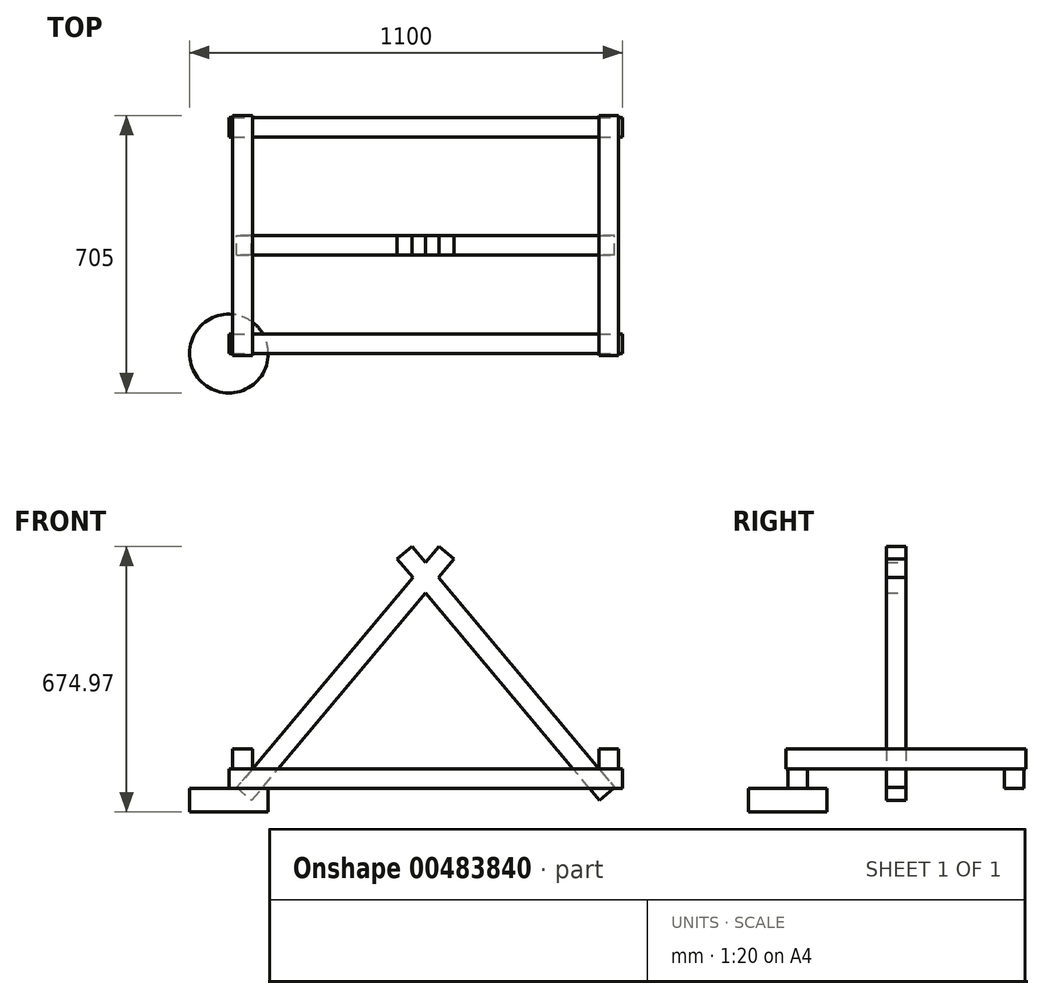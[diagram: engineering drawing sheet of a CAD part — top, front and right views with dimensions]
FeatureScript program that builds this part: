
annotation { "Feature Type Name" : "Feature", "Feature Type Description" : "" }
export const myFeature = defineFeature(function(context is Context, id is Id, definition is map)
    precondition{}
    {
        {
            var Q0;
            Q0=qCreatedBy(makeId("Top.planeOp"),FACE);
            var sketch = newSketch(context, id + "F0", { "sketchPlane" : qUnion([Q0])});
            skLineSegment(sketch, "E0.bottom", {"start": v(-500, 300) * mm, "end": v(500, 300) * mm});
            skLineSegment(sketch, "E0.top", {"start": v(-500, 250) * mm, "end": v(500, 250) * mm});
            skLineSegment(sketch, "E0.left", {"start": v(-500, 300) * mm, "end": v(-500, 250) * mm});
            skLineSegment(sketch, "E0.right", {"start": v(500, 300) * mm, "end": v(500, 250) * mm});
            skLineSegment(sketch, "E1.MirrorCS", {"start": v(500, -300) * mm, "end": v(500, -250) * mm});
            skLineSegment(sketch, "E2.MirrorCS", {"start": v(-500, -300) * mm, "end": v(-500, -250) * mm});
            skLineSegment(sketch, "E3.MirrorCS", {"start": v(-500, -300) * mm, "end": v(500, -300) * mm});
            skLineSegment(sketch, "E4.MirrorCS", {"start": v(-500, -250) * mm, "end": v(500, -250) * mm});
            skSolve(sketch);
        }
        {
            var Q0;
            Q0=makeQuery(id+"F0.imprint","IMPRINT",FACE,{"disambiguationData":[TD([[makeQuery(id+"F0.imprint","IMPRINT",EDGE,{"derivedFrom":sQuery(id+"F0.wireOp",EDGE,"E0.bottom")}),-1.0]])]});
            var Q1;
            Q1=makeQuery(id+"F0.imprint","IMPRINT",FACE,{"disambiguationData":[TD([[makeQuery(id+"F0.imprint","IMPRINT",EDGE,{"derivedFrom":sQuery(id+"F0.wireOp",EDGE,"E1.MirrorCS")}),1.0]])]});
            extrude(context, id + "F1", {"entities" : qUnion([Q0, Q1]), "depth" : 50 * mm});
        }
        {
            var Q0;
            Q0=makeQuery(id+"F1.opExtrude","CAP_FACE",FACE,{"disambiguationData":[OSD([sQuery(id+"F0.wireOp",EDGE,"E0.bottom"),sQuery(id+"F0.wireOp",EDGE,"E0.top"),sQuery(id+"F0.wireOp",EDGE,"E0.left"),sQuery(id+"F0.wireOp",EDGE,"E0.right")])],"isStart":false});
            var sketch = newSketch(context, id + "F2", { "sketchPlane" : qUnion([Q0])});
            skLineSegment(sketch, "E5.bottom", {"start": v(440, 305) * mm, "end": v(490, 305) * mm});
            skLineSegment(sketch, "E5.top", {"start": v(440, -305) * mm, "end": v(490, -305) * mm});
            skLineSegment(sketch, "E5.left", {"start": v(440, 305) * mm, "end": v(440, -305) * mm});
            skLineSegment(sketch, "E5.right", {"start": v(490, 305) * mm, "end": v(490, -305) * mm});
            skLineSegment(sketch, "E6.MirrorCS", {"start": v(-440, 305) * mm, "end": v(-440, -305) * mm});
            skLineSegment(sketch, "E7.MirrorCS", {"start": v(-490, 305) * mm, "end": v(-490, -305) * mm});
            skLineSegment(sketch, "E8.MirrorCS", {"start": v(-440, -305) * mm, "end": v(-490, -305) * mm});
            skLineSegment(sketch, "E9.MirrorCS", {"start": v(-440, 305) * mm, "end": v(-490, 305) * mm});
            skSolve(sketch);
        }
        {
            var Q0;
            {var subQ0=sQuery(id+"F2.wireOp",EDGE,"E8.MirrorCS");Q0=makeQuery(id+"F2.imprint","IMPRINT",FACE,{"disambiguationData":[TD([[makeQuery(id+"F2.imprint","IMPRINT",EDGE,{"derivedFrom":subQ0}),-1.0]])]});}
            var Q1;
            {var subQ0=sQuery(id+"F2.wireOp",EDGE,"E5.top");Q1=makeQuery(id+"F2.imprint","IMPRINT",FACE,{"disambiguationData":[TD([[makeQuery(id+"F2.imprint","IMPRINT",EDGE,{"derivedFrom":subQ0}),1.0]])]});}
            var Q2;
            {var subQ0=sQuery(id+"F2.wireOp",EDGE,"E6.MirrorCS");var subQ1=makeQuery(id+"F1.opExtrude","CAP_EDGE",EDGE,{"disambiguationData":[OSD([sQuery(id+"F0.wireOp",EDGE,"E0.bottom")])],"isStart":false});var subQ2=makeQuery(id+"F2.imprint","INTERSECT",VERTEX,{"derivedFrom":[subQ1,subQ0]});Q2=makeQuery(id+"F2.imprint","IMPRINT",FACE,{"disambiguationData":[TD([[makeQuery(id+"F2.imprint","IMPRINT",EDGE,{"disambiguationData":[TD([[subQ2,-1.0]])],"derivedFrom":subQ0}),-1.0]])]});}
            var Q3;
            {var subQ0=sQuery(id+"F2.wireOp",EDGE,"E5.left");var subQ1=makeQuery(id+"F1.opExtrude","CAP_EDGE",EDGE,{"disambiguationData":[OSD([sQuery(id+"F0.wireOp",EDGE,"E0.bottom")])],"isStart":false});var subQ2=makeQuery(id+"F2.imprint","INTERSECT",VERTEX,{"derivedFrom":[subQ1,subQ0]});Q3=makeQuery(id+"F2.imprint","IMPRINT",FACE,{"disambiguationData":[TD([[makeQuery(id+"F2.imprint","IMPRINT",EDGE,{"disambiguationData":[TD([[subQ2,-1.0]])],"derivedFrom":subQ0}),1.0]])]});}
            var Q4;
            {var subQ0=sQuery(id+"F2.wireOp",EDGE,"E9.MirrorCS");Q4=makeQuery(id+"F2.imprint","IMPRINT",FACE,{"disambiguationData":[TD([[makeQuery(id+"F2.imprint","IMPRINT",EDGE,{"derivedFrom":subQ0}),1.0]])]});}
            var Q5;
            {var subQ0=sQuery(id+"F2.wireOp",EDGE,"E5.bottom");Q5=makeQuery(id+"F2.imprint","IMPRINT",FACE,{"disambiguationData":[TD([[makeQuery(id+"F2.imprint","IMPRINT",EDGE,{"derivedFrom":subQ0}),-1.0]])]});}
            extrude(context, id + "F3", {"entities" : qUnion([Q0, Q1, Q2, Q3, Q4, Q5]), "operationType" : NewBodyOperationType.ADD, "depth" : 50 * mm});
        }
        {
            var Q0;
            Q0=qCreatedBy(makeId("Front.planeOp"),FACE);
            var sketch = newSketch(context, id + "F4", { "sketchPlane" : qUnion([Q0])});
            skLineSegment(sketch, "E10", {"start": v(34.07, 614.97) * mm, "end": v(-480.16, 2.14) * mm});
            skLineSegment(sketch, "E11", {"start": v(-480.16, 2.14) * mm, "end": v(-441.86, -30) * mm});
            skLineSegment(sketch, "E12", {"start": v(-441.86, -30) * mm, "end": v(72.37, 582.84) * mm});
            skLineSegment(sketch, "E13", {"start": v(72.37, 582.84) * mm, "end": v(34.07, 614.97) * mm});
            skLineSegment(sketch, "E14.MirrorCS", {"start": v(441.86, -30) * mm, "end": v(-72.37, 582.84) * mm});
            skLineSegment(sketch, "E15.MirrorCS", {"start": v(-34.07, 614.97) * mm, "end": v(480.16, 2.14) * mm});
            skLineSegment(sketch, "E16.MirrorCS", {"start": v(480.16, 2.14) * mm, "end": v(441.86, -30) * mm});
            skLineSegment(sketch, "E17.MirrorCS", {"start": v(-72.37, 582.84) * mm, "end": v(-34.07, 614.97) * mm});
            skSolve(sketch);
        }
        {
            var Q0;
            {var subQ0=sQuery(id+"F4.wireOp",EDGE,"E13");Q0=makeQuery(id+"F4.imprint","IMPRINT",FACE,{"disambiguationData":[TD([[makeQuery(id+"F4.imprint","IMPRINT",EDGE,{"derivedFrom":subQ0}),1.0]])]});}
            var Q1;
            {var subQ5=sQuery(id+"F4.wireOp",EDGE,"E17.MirrorCS");Q1=makeQuery(id+"F4.imprint","IMPRINT",FACE,{"disambiguationData":[TD([[makeQuery(id+"F4.imprint","IMPRINT",EDGE,{"derivedFrom":subQ5}),-1.0]])]});}
            var Q2;
            {var subQ0=sQuery(id+"F4.wireOp",EDGE,"E15.MirrorCS");var subQ1=sQuery(id+"F4.wireOp",EDGE,"E10");var subQ2=makeQuery(id+"F4.imprint","INTERSECT",VERTEX,{"derivedFrom":[subQ1,subQ0]});Q2=makeQuery(id+"F4.imprint","IMPRINT",FACE,{"disambiguationData":[TD([[makeQuery(id+"F4.imprint","IMPRINT",EDGE,{"disambiguationData":[TD([[subQ2,-1.0]])],"derivedFrom":subQ1}),1.0]])]});}
            var Q3;
            {var subQ0=sQuery(id+"F4.wireOp",EDGE,"E11");Q3=makeQuery(id+"F4.imprint","IMPRINT",FACE,{"disambiguationData":[TD([[makeQuery(id+"F4.imprint","IMPRINT",EDGE,{"derivedFrom":subQ0}),1.0]])]});}
            var Q4;
            {var subQ5=sQuery(id+"F4.wireOp",EDGE,"E16.MirrorCS");Q4=makeQuery(id+"F4.imprint","IMPRINT",FACE,{"disambiguationData":[TD([[makeQuery(id+"F4.imprint","IMPRINT",EDGE,{"derivedFrom":subQ5}),-1.0]])]});}
            var Q5;
            Q5=makeQuery(id+"F1.opExtrude","SWEPT_FACE",FACE,{"disambiguationData":[OSD([sQuery(id+"F0.wireOp",EDGE,"E4.MirrorCS")])]});
            extrude(context, id + "F5", {"entities" : qUnion([Q0, Q1, Q2, Q3, Q4]), "depth" : 50 * mm});
        }
        {
            var Q0;
            Q0=qCreatedBy(makeId("Top.planeOp"),FACE);
            var sketch = newSketch(context, id + "F6", { "sketchPlane" : qUnion([Q0])});
            skCircle(sketch, "E18", {"center": v(-500, -300) * mm, "radius": 100 * mm});
            skSolve(sketch);
        }
        {
            var Q0;
            Q0=makeQuery(id+"F6.imprint","IMPRINT",FACE,{"disambiguationData":[TD([[makeQuery(id+"F6.imprint","IMPRINT",EDGE,{"derivedFrom":sQuery(id+"F6.wireOp",EDGE,"E18")}),1.0]])]});
            extrude(context, id + "F7", {"entities" : qUnion([Q0]), "oppositeDirection" : true, "depth" : 60 * mm});
        }
    });
